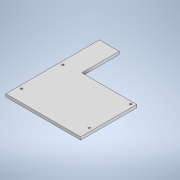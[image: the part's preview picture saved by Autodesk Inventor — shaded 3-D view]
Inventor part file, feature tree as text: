
AUTODESK INVENTOR PART (.ipt)
format: ipt  version: 2020 (Build 240168000, 168)  size: 131,584 bytes
history: native  units: mm
features: other x2, sketch x2, extrude x1, hole x1, projected_geometry x1
ambient origin geometry x8: Origin, YZ Plane, XZ Plane, XY Plane, X Axis, Y Axis, Z Axis, Center Point
bodies: Body1 (feature_tree)
feature tree (7):
  other  "작업 평면1"
  extrude  "돌출1"  Depth=5.0mm TaperAngle=0.0deg
  hole  "구멍1"  [1 undecoded]
  sketch  "스케치1"
  sketch  "스케치2"
  projected_geometry  "투영된 루프2"
  other  "솔리드1"
note: 1 required parameter value undecoded (feature->parameter linkage not recoverable at this tier; creation-order binding heuristic only, values carry confidence <= 0.55)
